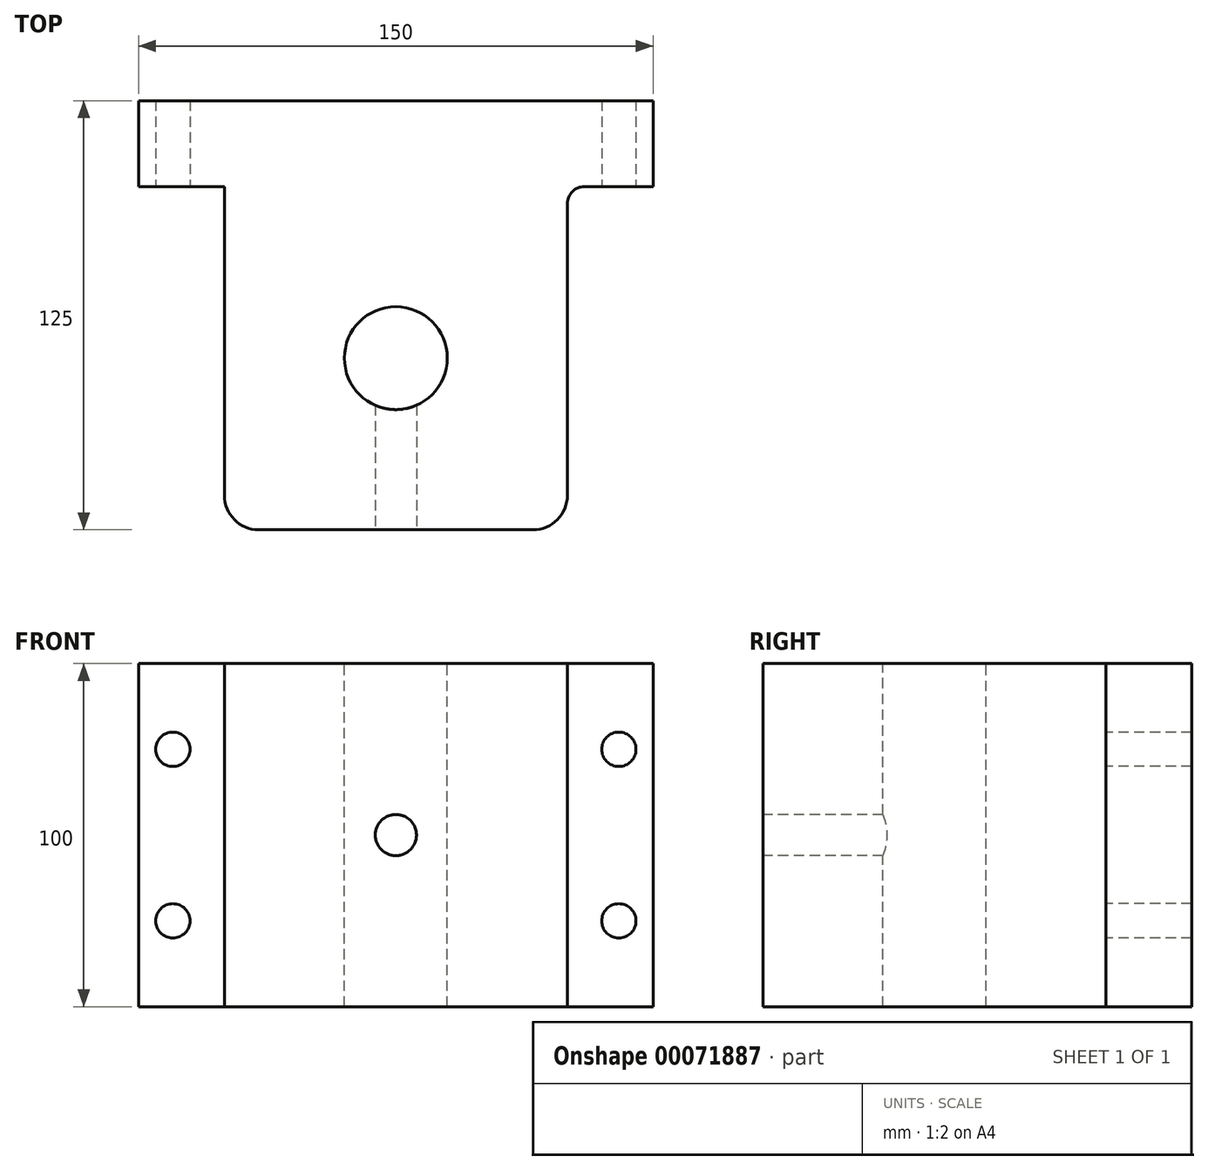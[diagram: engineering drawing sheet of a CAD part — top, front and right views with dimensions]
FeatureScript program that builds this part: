
annotation { "Feature Type Name" : "Feature", "Feature Type Description" : "" }
export const myFeature = defineFeature(function(context is Context, id is Id, definition is map)
    precondition{}
    {
        {
            var Q0;
            Q0=qCreatedBy(makeId("Front.planeOp"),FACE);
            var sketch = newSketch(context, id + "F0", { "sketchPlane" : qUnion([Q0])});
            skLineSegment(sketch, "E0.bottom", {"start": v(-50, -50) * mm, "end": v(50, -50) * mm});
            skLineSegment(sketch, "E0.top", {"start": v(-50, 50) * mm, "end": v(50, 50) * mm});
            skLineSegment(sketch, "E0.left", {"start": v(-50, -50) * mm, "end": v(-50, 50) * mm});
            skLineSegment(sketch, "E0.right", {"start": v(50, -50) * mm, "end": v(50, 50) * mm});
            skPoint(sketch, "E0.middle", {"position": v(0, 0) * mm});
            skSolve(sketch);
        }
        {
            var Q0;
            Q0=makeQuery(id+"F0.imprint","IMPRINT",FACE,{"disambiguationData":[TD([[makeQuery(id+"F0.imprint","IMPRINT",EDGE,{"derivedFrom":sQuery(id+"F0.wireOp",EDGE,"E0.bottom")}),1.0]])]});
            extrude(context, id + "F1", {"entities" : qUnion([Q0]), "depth" : 100 * mm});
        }
        {
            var Q0;
            Q0=makeQuery(id+"F1.opExtrude","CAP_EDGE",EDGE,{"disambiguationData":[OSD([sQuery(id+"F0.wireOp",EDGE,"E0.right")])],"isStart":false});
            var Q1;
            Q1=makeQuery(id+"F1.opExtrude","CAP_EDGE",EDGE,{"disambiguationData":[OSD([sQuery(id+"F0.wireOp",EDGE,"E0.left")])],"isStart":false});
            fillet(context, id + "F2", {"entities" : qUnion([Q0, Q1]), "radius" : 10 * mm, "tangentPropagation" : true, "allowEdgeOverflow" : false});
        }
        {
            var Q0;
            Q0=makeQuery(id+"F1.opExtrude","SWEPT_FACE",FACE,{"disambiguationData":[OSD([sQuery(id+"F0.wireOp",EDGE,"E0.top")])]});
            var sketch = newSketch(context, id + "F3", { "sketchPlane" : qUnion([Q0])});
            skCircle(sketch, "E1", {"center": v(0, -50) * mm, "radius": 15 * mm});
            skSolve(sketch);
        }
        {
            var Q0;
            Q0=makeQuery(id+"F3.imprint","IMPRINT",FACE,{"disambiguationData":[TD([[makeQuery(id+"F3.imprint","IMPRINT",EDGE,{"derivedFrom":sQuery(id+"F3.wireOp",EDGE,"E1")}),1.0]])]});
            extrude(context, id + "F4", {"entities" : qUnion([Q0]), "operationType" : NewBodyOperationType.REMOVE, "endBound" : BoundingType.THROUGH_ALL, "oppositeDirection" : true, "depth" : 25 * mm});
        }
        {
            var Q0;
            Q0=makeQuery(id+"F1.opExtrude","CAP_FACE",FACE,{"disambiguationData":[OSD([sQuery(id+"F0.wireOp",EDGE,"E0.bottom"),sQuery(id+"F0.wireOp",EDGE,"E0.top"),sQuery(id+"F0.wireOp",EDGE,"E0.left"),sQuery(id+"F0.wireOp",EDGE,"E0.right")])],"isStart":false});
            var sketch = newSketch(context, id + "F5", { "sketchPlane" : qUnion([Q0])});
            skCircle(sketch, "E2", {"center": v(0, 0) * mm, "radius": 6 * mm});
            skSolve(sketch);
        }
        {
            var Q0;
            Q0 = qSketchRegion(id + "F5", true);
            extrude(context, id + "F6", {"entities" : qUnion([Q0]), "operationType" : NewBodyOperationType.REMOVE, "endBound" : BoundingType.UP_TO_NEXT, "oppositeDirection" : true, "depth" : 25 * mm});
        }
        {
            var Q0;
            Q0=qCreatedBy(makeId("Front.planeOp"),FACE);
            var sketch = newSketch(context, id + "F7", { "sketchPlane" : qUnion([Q0])});
            skLineSegment(sketch, "E3.bottom", {"start": v(-75, -50) * mm, "end": v(75, -50) * mm});
            skLineSegment(sketch, "E3.top", {"start": v(-75, 50) * mm, "end": v(75, 50) * mm});
            skLineSegment(sketch, "E3.left", {"start": v(-75, -50) * mm, "end": v(-75, 50) * mm});
            skLineSegment(sketch, "E3.right", {"start": v(75, -50) * mm, "end": v(75, 50) * mm});
            skPoint(sketch, "E3.middle", {"position": v(0, 0) * mm});
            skSolve(sketch);
        }
        {
            var Q0;
            Q0 = qSketchRegion(id + "F7", true);
            extrude(context, id + "F8", {"entities" : qUnion([Q0]), "operationType" : NewBodyOperationType.ADD, "oppositeDirection" : true, "depth" : 25 * mm});
        }
        {
            var Q0;
            Q0=makeQuery(id+"F1.opExtrude","CAP_EDGE",EDGE,{"disambiguationData":[OSD([sQuery(id+"F0.wireOp",EDGE,"E0.right")])],"isStart":true});
            var Q1;
            Q1=makeQuery(id+"F1.opExtrude","CAP_EDGE",EDGE,{"disambiguationData":[OSD([sQuery(id+"F0.wireOp",EDGE,"E0.left")])],"isStart":true});
            fillet(context, id + "F9", {"entities" : qUnion([Q0, Q1]), "radius" : 5 * mm, "tangentPropagation" : true, "allowEdgeOverflow" : false});
        }
        {
            var Q0;
            Q0=qCreatedBy(makeId("Front.planeOp"),FACE);
            var sketch = newSketch(context, id + "F10", { "sketchPlane" : qUnion([Q0])});
            skLineSegment(sketch, "E4", {"start": v(-74.97, 25) * mm, "end": v(74.82, 25) * mm, "construction": true});
            skLineSegment(sketch, "E5", {"start": v(-74.97, -25) * mm, "end": v(74.82, -25) * mm, "construction": true});
            skLineSegment(sketch, "E6", {"start": v(65, 61.74) * mm, "end": v(65, -59.35) * mm, "construction": true});
            skLineSegment(sketch, "E7", {"start": v(-65, 57.88) * mm, "end": v(-65, -56.3) * mm, "construction": true});
            skPoint(sketch, "E8", {"position": v(-65, 25) * mm});
            skPoint(sketch, "E9", {"position": v(65, 25) * mm});
            skPoint(sketch, "E10", {"position": v(-65, -25) * mm});
            skPoint(sketch, "E11", {"position": v(65, -25) * mm});
            skSolve(sketch);
        }
        {
            var Q0;
            Q0=sQuery(id+"F10.wireOp",VERTEX,"E8");
            var Q1;
            Q1=sQuery(id+"F10.wireOp",VERTEX,"E10");
            var Q2;
            Q2=sQuery(id+"F10.wireOp",VERTEX,"E9");
            var Q3;
            Q3=sQuery(id+"F10.wireOp",VERTEX,"E11");
            var Q4;
            Q4=makeQuery(id+"F1.opExtrude","SWEPT_BODY",BODY,{"disambiguationData":[OSD([sQuery(id+"F0.wireOp",EDGE,"E0.bottom"),sQuery(id+"F0.wireOp",EDGE,"E0.top"),sQuery(id+"F0.wireOp",EDGE,"E0.left"),sQuery(id+"F0.wireOp",EDGE,"E0.right")])]});
            hole(context, id + "F11", {"style" : HoleStyle.SIMPLE, "holeDiameter" : 10 * mm, "endStyle" : HoleEndStyle.THROUGH, "locations" : qUnion([Q0, Q1, Q2, Q3]), "scope" : qUnion([Q4])});
        }
    });
